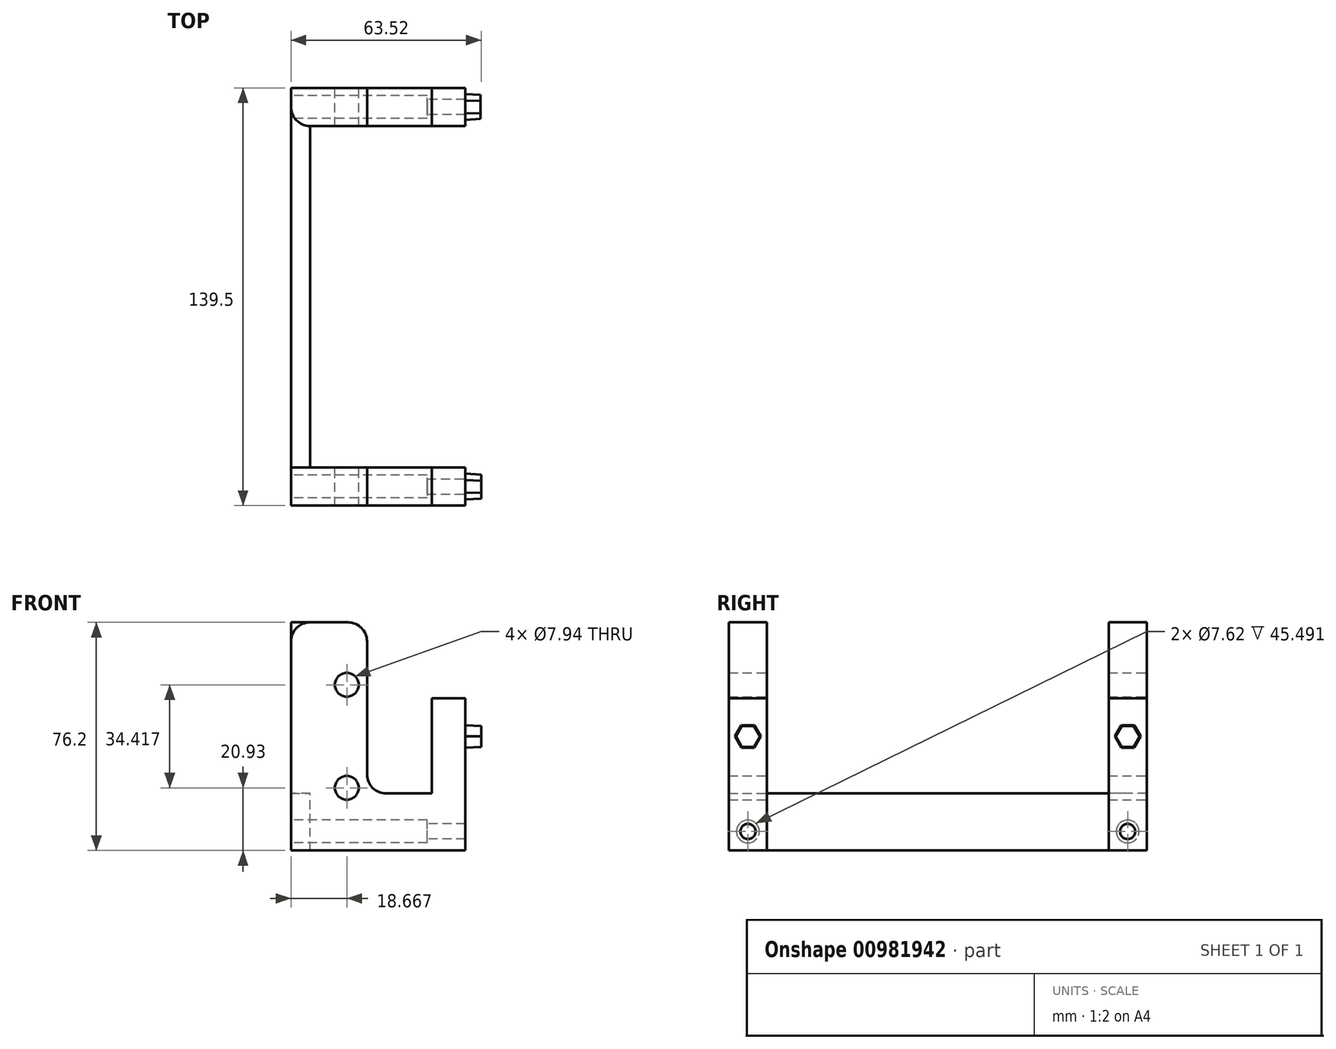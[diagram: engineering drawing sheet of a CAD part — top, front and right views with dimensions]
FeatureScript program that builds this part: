
annotation { "Feature Type Name" : "Feature", "Feature Type Description" : "" }
export const myFeature = defineFeature(function(context is Context, id is Id, definition is map)
    precondition{}
    {
        {
            var Q0;
            Q0=qCreatedBy(makeId("Right.planeOp"),FACE);
            var sketch = newSketch(context, id + "F0", { "sketchPlane" : qUnion([Q0])});
            skLineSegment(sketch, "E0.bottom", {"start": v(0, 50.8) * mm, "end": v(12.7, 50.8) * mm});
            skLineSegment(sketch, "E0.top", {"start": v(0, 0) * mm, "end": v(12.7, 0) * mm});
            skLineSegment(sketch, "E0.left", {"start": v(0, 50.8) * mm, "end": v(0, 0) * mm});
            skLineSegment(sketch, "E0.right", {"start": v(12.7, 50.8) * mm, "end": v(12.7, 0) * mm});
            skSolve(sketch);
        }
        {
            var Q0;
            Q0=qSketchRegion(id+"F0",true);
            extrude(context, id + "F1", {"entities" : qUnion([Q0]), "depth" : 11.1 * mm, "offsetDistance" : 25.4 * mm});
        }
        {
            var Q0;
            Q0=makeQuery(id+"F1.opExtrude","CAP_FACE",FACE,{"disambiguationData":[OSD([sQuery(id+"F0.wireOp",EDGE,"E0.bottom"),sQuery(id+"F0.wireOp",EDGE,"E0.top"),sQuery(id+"F0.wireOp",EDGE,"E0.left"),sQuery(id+"F0.wireOp",EDGE,"E0.right")])],"isStart":false});
            var sketch = newSketch(context, id + "F2", { "sketchPlane" : qUnion([Q0])});
            skCircle(sketch, "E1.cCircle", {"center": v(6.35, 38.1) * mm, "radius": 3.74 * mm, "construction": true});
            skLineSegment(sketch, "E1.0", {"start": v(8.5, 34.36) * mm, "end": v(4.2, 34.36) * mm});
            skLineSegment(sketch, "E1.1", {"start": v(4.2, 34.36) * mm, "end": v(2.03, 38.1) * mm});
            skLineSegment(sketch, "E1.2", {"start": v(2.03, 38.1) * mm, "end": v(4.2, 41.84) * mm});
            skLineSegment(sketch, "E1.3", {"start": v(4.2, 41.84) * mm, "end": v(8.5, 41.84) * mm});
            skLineSegment(sketch, "E1.4", {"start": v(8.5, 41.84) * mm, "end": v(10.67, 38.1) * mm});
            skLineSegment(sketch, "E1.5", {"start": v(10.67, 38.1) * mm, "end": v(8.5, 34.36) * mm});
            skPoint(sketch, "E1.0.midPoint", {"position": v(6.35, 34.36) * mm});
            skLineSegment(sketch, "E2", {"start": v(6.35, 38.1) * mm, "end": v(6.35, 50.8) * mm, "construction": true});
            skSolve(sketch);
        }
        {
            var Q0;
            Q0=qSketchRegion(id+"F2",true);
            extrude(context, id + "F3", {"entities" : qUnion([Q0]), "operationType" : NewBodyOperationType.ADD, "depth" : 5.08 * mm, "offsetDistance" : 25.4 * mm, "hasDraft" : true, "draftAngle" : 3 * degree, "draftPullDirection" : true});
        }
        {
            var Q0;
            Q0=makeQuery(id+"F1.opExtrude","CAP_FACE",FACE,{"disambiguationData":[OSD([sQuery(id+"F0.wireOp",EDGE,"E0.bottom"),sQuery(id+"F0.wireOp",EDGE,"E0.top"),sQuery(id+"F0.wireOp",EDGE,"E0.left"),sQuery(id+"F0.wireOp",EDGE,"E0.right")])],"isStart":true});
            var sketch = newSketch(context, id + "F4", { "sketchPlane" : qUnion([Q0])});
            skLineSegment(sketch, "E3.bottom", {"start": v(-12.7, 0) * mm, "end": v(0, 0) * mm});
            skLineSegment(sketch, "E3.top", {"start": v(-12.7, 19.05) * mm, "end": v(0, 19.05) * mm});
            skLineSegment(sketch, "E3.left", {"start": v(-12.7, 0) * mm, "end": v(-12.7, 19.05) * mm});
            skLineSegment(sketch, "E3.right", {"start": v(0, 0) * mm, "end": v(0, 19.05) * mm});
            skSolve(sketch);
        }
        {
            var Q0;
            Q0=qSketchRegion(id+"F4",true);
            extrude(context, id + "F5", {"entities" : qUnion([Q0]), "operationType" : NewBodyOperationType.ADD, "depth" : 47.1 * mm, "offsetDistance" : 25.4 * mm});
        }
        {
            var Q0;
            Q0=makeQuery(id+"F5.boolean.opBoolean","MERGE",FACE,{"derivedFrom":[makeQuery(id+"F1.opExtrude","SWEPT_FACE",FACE,{"disambiguationData":[OSD([sQuery(id+"F0.wireOp",EDGE,"E0.left")])]}),makeQuery(id+"F5.opExtrude","SWEPT_FACE",FACE,{"disambiguationData":[OSD([sQuery(id+"F4.wireOp",EDGE,"E3.right")])]})]});
            var sketch = newSketch(context, id + "F6", { "sketchPlane" : qUnion([Q0])});
            skLineSegment(sketch, "E4.bottom", {"start": v(-47.1, 0) * mm, "end": v(-40.74, 0) * mm});
            skLineSegment(sketch, "E4.left", {"start": v(-47.1, 0) * mm, "end": v(-47.1, 19.05) * mm});
            skLineSegment(sketch, "E4.right", {"start": v(-40.74, 0) * mm, "end": v(-40.74, 19.05) * mm});
            skLineSegment(sketch, "E5", {"start": v(-47.1, 19.05) * mm, "end": v(-40.74, 19.05) * mm});
            skSolve(sketch);
        }
        {
            var Q0;
            Q0=qSketchRegion(id+"F6",true);
            extrude(context, id + "F7", {"entities" : qUnion([Q0]), "operationType" : NewBodyOperationType.ADD, "depth" : 126.8 * mm, "offsetDistance" : 25.4 * mm});
        }
        {
            var Q0;
            Q0=makeQuery(id+"F7.opExtrude","SWEPT_FACE",FACE,{"disambiguationData":[OSD([sQuery(id+"F6.wireOp",EDGE,"E4.right")])]});
            var sketch = newSketch(context, id + "F8", { "sketchPlane" : qUnion([Q0])});
            skLineSegment(sketch, "E6.bottom", {"start": v(-126.8, 19.05) * mm, "end": v(-114.1, 19.05) * mm});
            skLineSegment(sketch, "E6.top", {"start": v(-126.8, 0) * mm, "end": v(-114.1, 0) * mm});
            skLineSegment(sketch, "E6.left", {"start": v(-126.8, 19.05) * mm, "end": v(-126.8, 0) * mm});
            skLineSegment(sketch, "E6.right", {"start": v(-114.1, 19.05) * mm, "end": v(-114.1, 0) * mm});
            skSolve(sketch);
        }
        {
            var Q0;
            Q0 = qSketchRegion(id + "F8", true);
            var Q1;
            Q1=makeQuery(id+"F1.opExtrude","CAP_FACE",FACE,{"disambiguationData":[OSD([sQuery(id+"F0.wireOp",EDGE,"E0.bottom"),sQuery(id+"F0.wireOp",EDGE,"E0.top"),sQuery(id+"F0.wireOp",EDGE,"E0.left"),sQuery(id+"F0.wireOp",EDGE,"E0.right")])],"isStart":true});
            extrude(context, id + "F9", {"entities" : qUnion([Q0]), "operationType" : NewBodyOperationType.ADD, "endBound" : BoundingType.UP_TO_SURFACE, "depth" : 13.97 * mm, "endBoundEntityFace" : qUnion([Q1]), "offsetDistance" : 25.4 * mm});
        }
        {
            var Q0;
            Q0=makeQuery(id+"F9.opExtrude","CAP_FACE",FACE,{"disambiguationData":[OSD([sQuery(id+"F8.wireOp",EDGE,"E6.bottom"),sQuery(id+"F8.wireOp",EDGE,"E6.top"),sQuery(id+"F8.wireOp",EDGE,"E6.left"),sQuery(id+"F8.wireOp",EDGE,"E6.right")])],"isStart":false});
            var sketch = newSketch(context, id + "F10", { "sketchPlane" : qUnion([Q0])});
            skLineSegment(sketch, "E7.bottom", {"start": v(-114.1, 0) * mm, "end": v(-126.8, 0) * mm});
            skLineSegment(sketch, "E7.top", {"start": v(-114.1, 50.8) * mm, "end": v(-126.8, 50.8) * mm});
            skLineSegment(sketch, "E7.left", {"start": v(-114.1, 0) * mm, "end": v(-114.1, 50.8) * mm});
            skLineSegment(sketch, "E7.right", {"start": v(-126.8, 0) * mm, "end": v(-126.8, 50.8) * mm});
            skSolve(sketch);
        }
        {
            var Q0;
            Q0 = qSketchRegion(id + "F10", true);
            extrude(context, id + "F11", {"entities" : qUnion([Q0]), "operationType" : NewBodyOperationType.ADD, "depth" : 11.1 * mm, "offsetDistance" : 25.4 * mm});
        }
        {
            var Q0;
            Q0=makeQuery(id+"F11.opExtrude","CAP_FACE",FACE,{"disambiguationData":[OSD([sQuery(id+"F10.wireOp",EDGE,"E7.bottom"),sQuery(id+"F10.wireOp",EDGE,"E7.top"),sQuery(id+"F10.wireOp",EDGE,"E7.left"),sQuery(id+"F10.wireOp",EDGE,"E7.right")])],"isStart":false});
            var sketch = newSketch(context, id + "F12", { "sketchPlane" : qUnion([Q0])});
            skCircle(sketch, "E8.cCircle", {"center": v(-120.45, 38.1) * mm, "radius": 3.74 * mm, "construction": true});
            skLineSegment(sketch, "E8.0", {"start": v(-122.6, 41.84) * mm, "end": v(-118.29, 41.84) * mm});
            skLineSegment(sketch, "E8.1", {"start": v(-118.29, 41.84) * mm, "end": v(-116.13, 38.1) * mm});
            skLineSegment(sketch, "E8.2", {"start": v(-116.13, 38.1) * mm, "end": v(-118.29, 34.36) * mm});
            skLineSegment(sketch, "E8.3", {"start": v(-118.29, 34.36) * mm, "end": v(-122.6, 34.36) * mm});
            skLineSegment(sketch, "E8.4", {"start": v(-122.6, 34.36) * mm, "end": v(-124.76, 38.1) * mm});
            skLineSegment(sketch, "E8.5", {"start": v(-124.76, 38.1) * mm, "end": v(-122.6, 41.84) * mm});
            skPoint(sketch, "E8.0.midPoint", {"position": v(-120.45, 41.84) * mm});
            skLineSegment(sketch, "E9", {"start": v(-120.45, 41.84) * mm, "end": v(-120.45, 50.8) * mm, "construction": true});
            skSolve(sketch);
        }
        {
            var Q0;
            Q0 = qSketchRegion(id + "F12", true);
            extrude(context, id + "F13", {"entities" : qUnion([Q0]), "operationType" : NewBodyOperationType.ADD, "depth" : 5.33 * mm, "offsetDistance" : 25.4 * mm, "hasDraft" : true, "draftAngle" : 3 * degree, "draftPullDirection" : true});
        }
        {
            var Q0;
            Q0=makeQuery(id+"F5.boolean.opBoolean","MERGE",FACE,{"derivedFrom":[makeQuery(id+"F1.opExtrude","SWEPT_FACE",FACE,{"disambiguationData":[OSD([sQuery(id+"F0.wireOp",EDGE,"E0.right")])]}),makeQuery(id+"F5.opExtrude","SWEPT_FACE",FACE,{"disambiguationData":[OSD([sQuery(id+"F4.wireOp",EDGE,"E3.left")])]})]});
            var sketch = newSketch(context, id + "F14", { "sketchPlane" : qUnion([Q0])});
            skLineSegment(sketch, "E10.bottom", {"start": v(21.7, 0) * mm, "end": v(47.1, 0) * mm});
            skLineSegment(sketch, "E10.top", {"start": v(21.7, 76.2) * mm, "end": v(47.1, 76.2) * mm});
            skLineSegment(sketch, "E10.left", {"start": v(21.7, 0) * mm, "end": v(21.7, 76.2) * mm});
            skLineSegment(sketch, "E10.right", {"start": v(47.1, 0) * mm, "end": v(47.1, 76.2) * mm});
            skSolve(sketch);
        }
        {
            var Q0;
            Q0 = qSketchRegion(id + "F14", true);
            var Q1;
            Q1=makeQuery(id+"F5.boolean.opBoolean","MERGE",FACE,{"derivedFrom":[makeQuery(id+"F1.opExtrude","SWEPT_FACE",FACE,{"disambiguationData":[OSD([sQuery(id+"F0.wireOp",EDGE,"E0.left")])]}),makeQuery(id+"F5.opExtrude","SWEPT_FACE",FACE,{"disambiguationData":[OSD([sQuery(id+"F4.wireOp",EDGE,"E3.right")])]})]});
            extrude(context, id + "F15", {"entities" : qUnion([Q0]), "operationType" : NewBodyOperationType.ADD, "endBound" : BoundingType.UP_TO_SURFACE, "oppositeDirection" : true, "depth" : 25.4 * mm, "endBoundEntityFace" : qUnion([Q1]), "offsetDistance" : 25.4 * mm});
        }
        {
            var Q0;
            Q0=makeQuery(id+"F11.boolean.opBoolean","MERGE",FACE,{"derivedFrom":[makeQuery(id+"F9.boolean.opBoolean","MERGE",FACE,{"derivedFrom":[makeQuery(id+"F7.opExtrude","CAP_FACE",FACE,{"disambiguationData":[OSD([sQuery(id+"F6.wireOp",EDGE,"E4.bottom"),sQuery(id+"F6.wireOp",EDGE,"E4.left"),sQuery(id+"F6.wireOp",EDGE,"E4.right"),sQuery(id+"F6.wireOp",EDGE,"E5")])],"isStart":false}),makeQuery(id+"F9.opExtrude","SWEPT_FACE",FACE,{"disambiguationData":[OSD([sQuery(id+"F8.wireOp",EDGE,"E6.left")])]})]}),makeQuery(id+"F11.opExtrude","SWEPT_FACE",FACE,{"disambiguationData":[OSD([sQuery(id+"F10.wireOp",EDGE,"E7.right")])]})]});
            var sketch = newSketch(context, id + "F16", { "sketchPlane" : qUnion([Q0])});
            skLineSegment(sketch, "E11.bottom", {"start": v(-47.1, 0) * mm, "end": v(-21.7, 0) * mm});
            skLineSegment(sketch, "E11.top", {"start": v(-47.1, 76.2) * mm, "end": v(-21.7, 76.2) * mm});
            skLineSegment(sketch, "E11.left", {"start": v(-47.1, 0) * mm, "end": v(-47.1, 76.2) * mm});
            skLineSegment(sketch, "E11.right", {"start": v(-21.7, 0) * mm, "end": v(-21.7, 76.2) * mm});
            skSolve(sketch);
        }
        {
            var Q0;
            Q0 = qSketchRegion(id + "F16", true);
            var Q1;
            Q1=makeQuery(id+"F11.boolean.opBoolean","MERGE",FACE,{"derivedFrom":[makeQuery(id+"F9.opExtrude","SWEPT_FACE",FACE,{"disambiguationData":[OSD([sQuery(id+"F8.wireOp",EDGE,"E6.right")])]}),makeQuery(id+"F11.opExtrude","SWEPT_FACE",FACE,{"disambiguationData":[OSD([sQuery(id+"F10.wireOp",EDGE,"E7.left")])]})]});
            extrude(context, id + "F17", {"entities" : qUnion([Q0]), "operationType" : NewBodyOperationType.ADD, "endBound" : BoundingType.UP_TO_SURFACE, "oppositeDirection" : true, "depth" : 25.4 * mm, "endBoundEntityFace" : qUnion([Q1]), "offsetDistance" : 25.4 * mm});
        }
        {
            var Q0;
            Q0=makeQuery(id+"F5.boolean.opBoolean","MERGE",FACE,{"derivedFrom":[makeQuery(id+"F1.opExtrude","SWEPT_FACE",FACE,{"disambiguationData":[OSD([sQuery(id+"F0.wireOp",EDGE,"E0.right")])]}),makeQuery(id+"F5.opExtrude","SWEPT_FACE",FACE,{"disambiguationData":[OSD([sQuery(id+"F4.wireOp",EDGE,"E3.left")])]})]});
            var sketch = newSketch(context, id + "F18", { "sketchPlane" : qUnion([Q0])});
            skCircle(sketch, "E12", {"center": v(28.42, 20.93) * mm, "radius": 3.97 * mm});
            skCircle(sketch, "E13", {"center": v(28.42, 55.35) * mm, "radius": 3.97 * mm});
            skSolve(sketch);
        }
        {
            var Q0;
            Q0 = qSketchRegion(id + "F18", true);
            extrude(context, id + "F19", {"entities" : qUnion([Q0]), "operationType" : NewBodyOperationType.REMOVE, "endBound" : BoundingType.THROUGH_ALL, "oppositeDirection" : true, "depth" : 25.4 * mm, "offsetDistance" : 25.4 * mm});
        }
        {
            var Q0;
            Q0=makeQuery(id+"F1.opExtrude","CAP_FACE",FACE,{"disambiguationData":[OSD([sQuery(id+"F0.wireOp",EDGE,"E0.bottom"),sQuery(id+"F0.wireOp",EDGE,"E0.top"),sQuery(id+"F0.wireOp",EDGE,"E0.left"),sQuery(id+"F0.wireOp",EDGE,"E0.right")])],"isStart":true});
            var sketch = newSketch(context, id + "F20", { "sketchPlane" : qUnion([Q0])});
            skCircle(sketch, "E14", {"center": v(-6.35, 6.35) * mm, "radius": 2.54 * mm});
            skPoint(sketch, "E14.centerSnap0", {"position": v(-6.35, 50.8) * mm});
            skSolve(sketch);
        }
        {
            var Q0;
            Q0=qSketchRegion(id+"F20",true);
            extrude(context, id + "F21", {"entities" : qUnion([Q0]), "operationType" : NewBodyOperationType.REMOVE, "endBound" : BoundingType.THROUGH_ALL, "oppositeDirection" : true, "depth" : 25.4 * mm, "offsetDistance" : 25.4 * mm});
        }
        {
            var Q0;
            Q0=makeQuery(id+"F11.opExtrude","CAP_FACE",FACE,{"disambiguationData":[OSD([sQuery(id+"F10.wireOp",EDGE,"E7.bottom"),sQuery(id+"F10.wireOp",EDGE,"E7.top"),sQuery(id+"F10.wireOp",EDGE,"E7.left"),sQuery(id+"F10.wireOp",EDGE,"E7.right")])],"isStart":false});
            var sketch = newSketch(context, id + "F22", { "sketchPlane" : qUnion([Q0])});
            skCircle(sketch, "E15", {"center": v(-120.45, 6.35) * mm, "radius": 2.54 * mm});
            skCircle(sketch, "E16", {"center": v(6.35, 6.35) * mm, "radius": 2.54 * mm});
            skSolve(sketch);
        }
        {
            var Q0;
            Q0 = qSketchRegion(id + "F22", true);
            extrude(context, id + "F23", {"entities" : qUnion([Q0]), "operationType" : NewBodyOperationType.REMOVE, "endBound" : BoundingType.THROUGH_ALL, "oppositeDirection" : true, "depth" : 25.4 * mm, "offsetDistance" : 25.4 * mm});
        }
        {
            var Q0;
            Q0=makeQuery(id+"F17.boolean.opBoolean","MERGE",FACE,{"derivedFrom":[makeQuery(id+"F15.boolean.opBoolean","MERGE",FACE,{"derivedFrom":[makeQuery(id+"F7.boolean.opBoolean","MERGE",FACE,{"derivedFrom":[makeQuery(id+"F5.opExtrude","CAP_FACE",FACE,{"disambiguationData":[OSD([sQuery(id+"F4.wireOp",EDGE,"E3.bottom"),sQuery(id+"F4.wireOp",EDGE,"E3.top"),sQuery(id+"F4.wireOp",EDGE,"E3.left"),sQuery(id+"F4.wireOp",EDGE,"E3.right")])],"isStart":false}),makeQuery(id+"F7.opExtrude","SWEPT_FACE",FACE,{"disambiguationData":[OSD([sQuery(id+"F6.wireOp",EDGE,"E4.left")])]})]}),makeQuery(id+"F15.opExtrude","SWEPT_FACE",FACE,{"disambiguationData":[OSD([sQuery(id+"F14.wireOp",EDGE,"E10.right")])]})]}),makeQuery(id+"F17.opExtrude","SWEPT_FACE",FACE,{"disambiguationData":[OSD([sQuery(id+"F16.wireOp",EDGE,"E11.left")])]})]});
            var sketch = newSketch(context, id + "F24", { "sketchPlane" : qUnion([Q0])});
            skCircle(sketch, "E17", {"center": v(120.45, 6.35) * mm, "radius": 3.81 * mm});
            skCircle(sketch, "E18", {"center": v(-6.35, 6.35) * mm, "radius": 3.81 * mm});
            skSolve(sketch);
        }
        {
            var Q0;
            Q0 = qSketchRegion(id + "F24", true);
            var Q1;
            Q1=makeQuery(id+"F1.opExtrude","CAP_FACE",FACE,{"disambiguationData":[OSD([sQuery(id+"F0.wireOp",EDGE,"E0.bottom"),sQuery(id+"F0.wireOp",EDGE,"E0.top"),sQuery(id+"F0.wireOp",EDGE,"E0.left"),sQuery(id+"F0.wireOp",EDGE,"E0.right")])],"isStart":false});
            extrude(context, id + "F25", {"entities" : qUnion([Q0]), "operationType" : NewBodyOperationType.REMOVE, "endBound" : BoundingType.UP_TO_SURFACE, "oppositeDirection" : true, "depth" : 25.4 * mm, "endBoundEntityFace" : qUnion([Q1]), "hasOffset" : true, "offsetDistance" : 12.7 * mm});
        }
        {
            var Q0;
            Q0=makeQuery(id+"F5.opExtrude","CAP_EDGE",EDGE,{"disambiguationData":[OSD([sQuery(id+"F4.wireOp",EDGE,"E3.top")])],"isStart":true});
            var Q1;
            Q1=makeQuery(id+"F15.boolean.opBoolean","INTERSECT",EDGE,{"derivedFrom":[makeQuery(id+"F9.boolean.opBoolean","MERGE",FACE,{"derivedFrom":[makeQuery(id+"F7.boolean.opBoolean","MERGE",FACE,{"derivedFrom":[makeQuery(id+"F5.opExtrude","SWEPT_FACE",FACE,{"disambiguationData":[OSD([sQuery(id+"F4.wireOp",EDGE,"E3.top")])]}),makeQuery(id+"F7.opExtrude","SWEPT_FACE",FACE,{"disambiguationData":[OSD([sQuery(id+"F6.wireOp",EDGE,"E5")])]})]}),makeQuery(id+"F9.opExtrude","SWEPT_FACE",FACE,{"disambiguationData":[OSD([sQuery(id+"F8.wireOp",EDGE,"E6.bottom")])]})]}),makeQuery(id+"F15.opExtrude","SWEPT_FACE",FACE,{"disambiguationData":[OSD([sQuery(id+"F14.wireOp",EDGE,"E10.left")])]})]});
            var Q2;
            {var subQ1=sQuery(id+"F4.wireOp",EDGE,"E3.top");var subQ3=sQuery(id+"F6.wireOp",EDGE,"E4.left");var subQ7=sQuery(id+"F6.wireOp",EDGE,"E5");Q2=makeQuery(id+"F17.boolean.opBoolean","INTERSECT",EDGE,{"derivedFrom":[makeQuery(id+"F15.boolean.opBoolean","SPLIT",FACE,{"disambiguationData":[TD([makeQuery(id+"F7.opExtrude","SWEPT_FACE",FACE,{"disambiguationData":[OSD([subQ3])]})])],"derivedFrom":makeQuery(id+"F9.boolean.opBoolean","MERGE",FACE,{"derivedFrom":[makeQuery(id+"F7.boolean.opBoolean","MERGE",FACE,{"derivedFrom":[makeQuery(id+"F5.opExtrude","SWEPT_FACE",FACE,{"disambiguationData":[OSD([subQ1])]}),makeQuery(id+"F7.opExtrude","SWEPT_FACE",FACE,{"disambiguationData":[OSD([subQ7])]})]}),makeQuery(id+"F9.opExtrude","SWEPT_FACE",FACE,{"disambiguationData":[OSD([sQuery(id+"F8.wireOp",EDGE,"E6.bottom")])]})]})}),makeQuery(id+"F17.opExtrude","SWEPT_FACE",FACE,{"disambiguationData":[OSD([sQuery(id+"F16.wireOp",EDGE,"E11.right")])]})]});}
            var Q3;
            Q3=makeQuery(id+"F9.opExtrude","CAP_EDGE",EDGE,{"disambiguationData":[OSD([sQuery(id+"F8.wireOp",EDGE,"E6.bottom")])],"isStart":false});
            var Q4;
            Q4=makeQuery(id+"F15.opExtrude","CAP_EDGE",EDGE,{"disambiguationData":[OSD([sQuery(id+"F14.wireOp",EDGE,"E10.right")])],"isStart":false});
            var Q5;
            Q5=makeQuery(id+"F15.opExtrude","SWEPT_EDGE",EDGE,{"disambiguationData":[OSD([sQuery(id+"F14.wireOp",EDGE,"E10.top"),sQuery(id+"F14.wireOp",EDGE,"E10.left")])]});
            var Q6;
            Q6=makeQuery(id+"F17.opExtrude","SWEPT_EDGE",EDGE,{"disambiguationData":[OSD([sQuery(id+"F16.wireOp",EDGE,"E11.top"),sQuery(id+"F16.wireOp",EDGE,"E11.left")])]});
            var Q7;
            Q7=makeQuery(id+"F17.opExtrude","SWEPT_EDGE",EDGE,{"disambiguationData":[OSD([sQuery(id+"F16.wireOp",EDGE,"E11.top"),sQuery(id+"F16.wireOp",EDGE,"E11.right")])]});
            fillet(context, id + "F26", {"entities" : qUnion([Q0, Q1, Q2, Q3, Q4, Q5, Q6, Q7]), "radius" : 6.35 * mm, "tangentPropagation" : true, "allowEdgeOverflow" : false});
        }
    });
